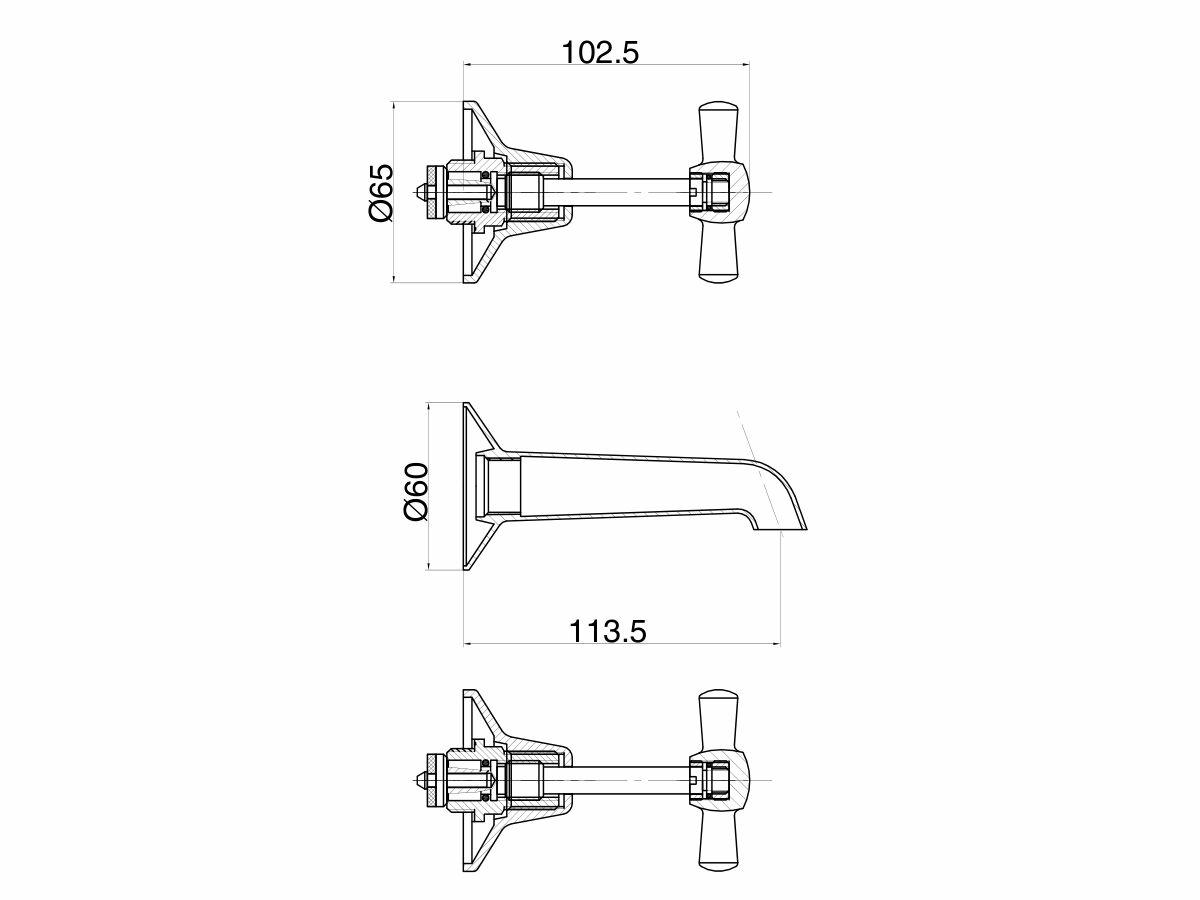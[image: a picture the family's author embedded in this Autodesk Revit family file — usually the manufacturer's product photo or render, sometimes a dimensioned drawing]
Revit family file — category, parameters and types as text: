
# Revit family: Reece_Tap_Base_Bath Set_Anti-Vandal
name_source: partatom
category: Plumbing Fixtures
revit_build: Autodesk Revit 2018 (Build: 20190510_1515(x64)
units: mm (PartAtom-declared; Revit-internal decimal feet)

## family parameters
Cut with Voids When Loaded = No
Host = Face
Part Type = Normal
Room Calculation Point = Yes
Round Connector Dimension = Use Diameter
Shared = Yes

## types (1)
- 113 mm_Chrome
    CWFU = 0
    Default Elevation = 0 mm  [stored 0 ft]
    Description = Base Bath Set Anti-Vandal Chrome
    Disclaimer = THIS FILE IS THE PROPERTY OF THE REECE GROUP. IT MAY NOT BE REPRODUCED, REVERSE-ENGINEERED OR MODIFIED. ANY REPUBLICATION, TRANSMISSION OR DISTRIBUTION FOR THE PURPOSE OF COMMERCIALLY EXPLOITING THE FILES IS PROHIBITED.
    HWFU = 0
    Keynote = Product #9505428, Reece_Tap_Base_Bath Set_Anti-Vandal - 113 mm_Chrome
    Manufacturer = Base
    Model = Base
    Reece_Detail_Additional = Anti-Vandal
    Reece_Detail_Disclaimer = THIS FILE IS THE PROPERTY OF THE REECE GROUP. IT MAY NOT BE REPRODUCED, REVERSE-ENGINEERED OR MODIFIED. ANY REPUBLICATION, TRANSMISSION OR DISTRIBUTION FOR THE PURPOSE OF COMMERCIALLY EXPLOITING THE FILES IS PROHIBITED.
    Reece_Detail_Shape = Bath Set
    Reece_Material-Main = Reece_Brass_Chrome
    Reece_Mixer_Height = 103 mm
    Reece_Product_Brand = Base
    Reece_Product_Description = Base Bath Set Anti-Vandal Chrome
    Reece_Product_Mount = Wall Mounted
    Reece_Product_Number = 9505428
    Reece_Product_Sub Brand = Base
    Reece_Product_Type = Tap
    Reece_Product_Web Page = https://www.reece.com.au
    Reece_Tap_Inlet = 12 mm  [stored 0.0393701 ft]
    Reece_Tap_Reach = 113 mm
    Type Comments = Tap
    URL = https://www.reece.com.au
    WFU = 0

note: [stored X ft] marks values corroborated as IEEE doubles in the binary element streams (Revit-internal decimal feet)

## geometry (parser evidence)
native form markers: Sweep x7
no freeform markers — native parametric forms only
